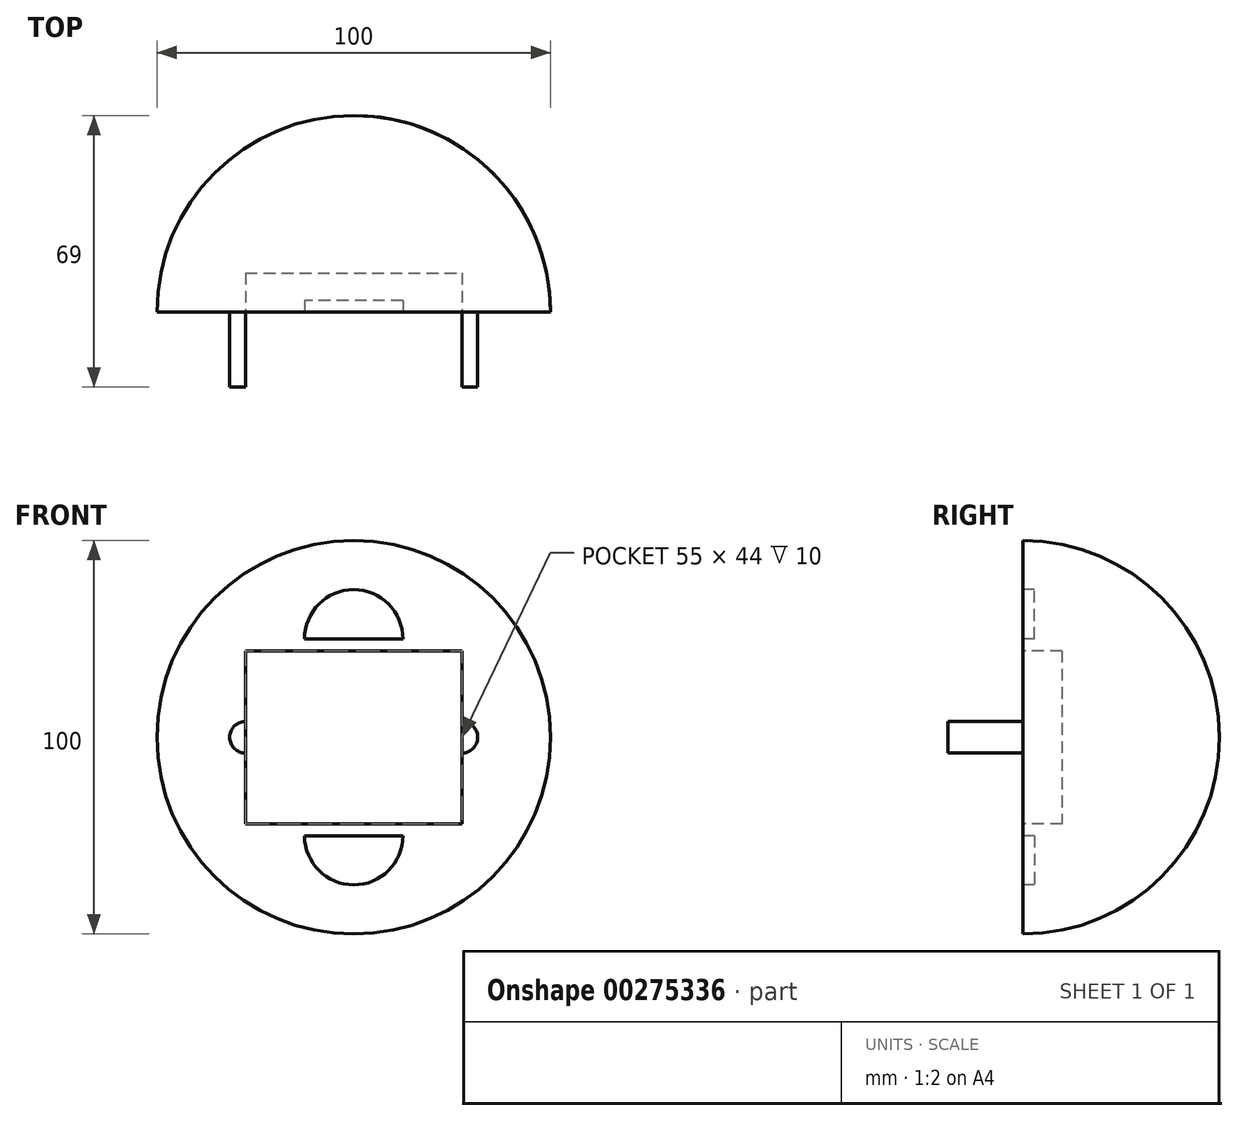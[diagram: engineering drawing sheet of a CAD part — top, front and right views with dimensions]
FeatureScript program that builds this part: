
annotation { "Feature Type Name" : "Feature", "Feature Type Description" : "" }
export const myFeature = defineFeature(function(context is Context, id is Id, definition is map)
    precondition{}
    {
        {
            var Q0;
            Q0=qCreatedBy(makeId("Top.planeOp"),FACE);
            var sketch = newSketch(context, id + "F0", { "sketchPlane" : qUnion([Q0])});
            skArc(sketch, "E0", {"start": v(0, 50) * mm, "mid": v(-35.36, 35.36) * mm, "end": v(-50, 0) * mm});
            skLineSegment(sketch, "E1", {"start": v(0, 50) * mm, "end": v(0, 0) * mm});
            skLineSegment(sketch, "E2", {"start": v(0, 0) * mm, "end": v(-50, 0) * mm});
            skSolve(sketch);
        }
        {
            var Q0;
            Q0=makeQuery(id+"F0.imprint","IMPRINT",FACE,{"disambiguationData":[TD([[makeQuery(id+"F0.imprint","IMPRINT",EDGE,{"derivedFrom":sQuery(id+"F0.wireOp",EDGE,"E0")}),1.0]])]});
            var Q1;
            Q1=sQuery(id+"F0.wireOp",EDGE,"E1");
            revolve(context, id + "F1", {"entities" : qUnion([Q0]), "axis" : qUnion([Q1]), "revolveType" : RevolveType.FULL});
        }
        {
            var Q0;
            Q0=qCreatedBy(makeId("Front.planeOp"),FACE);
            var sketch = newSketch(context, id + "F2", { "sketchPlane" : qUnion([Q0])});
            skLineSegment(sketch, "E3.bottom", {"start": v(-27.5, 22) * mm, "end": v(27.5, 22) * mm});
            skLineSegment(sketch, "E3.top", {"start": v(-27.5, -22) * mm, "end": v(27.5, -22) * mm});
            skLineSegment(sketch, "E3.left", {"start": v(-27.5, 22) * mm, "end": v(-27.5, -22) * mm});
            skLineSegment(sketch, "E3.right", {"start": v(27.5, 22) * mm, "end": v(27.5, -22) * mm});
            skPoint(sketch, "E3.middle", {"position": v(0, 0) * mm});
            skArc(sketch, "E4", {"start": v(-27.5, 4) * mm, "mid": v(-31.5, 0) * mm, "end": v(-27.5, -4) * mm});
            skPoint(sketch, "E5.center.orphan", {"position": v(27.5, 0) * mm});
            skArc(sketch, "E6", {"start": v(27.5, -4) * mm, "mid": v(31.5, 0) * mm, "end": v(27.5, 4) * mm});
            skSolve(sketch);
        }
        {
            var Q0;
            {var subQ4=sQuery(id+"F2.wireOp",EDGE,"E3.bottom");Q0=makeQuery(id+"F2.imprint","IMPRINT",FACE,{"disambiguationData":[TD([[makeQuery(id+"F2.imprint","IMPRINT",EDGE,{"derivedFrom":subQ4}),-1.0]])]});}
            extrude(context, id + "F3", {"entities" : qUnion([Q0]), "operationType" : NewBodyOperationType.REMOVE, "oppositeDirection" : true, "depth" : 10 * mm});
        }
        {
            var Q0;
            Q0=qCreatedBy(makeId("Front.planeOp"),FACE);
            var sketch = newSketch(context, id + "F4", { "sketchPlane" : qUnion([Q0])});
            skLineSegment(sketch, "E7", {"start": v(0, 0) * mm, "end": v(0, 25) * mm});
            skArc(sketch, "E8", {"start": v(12.5, 25) * mm, "mid": v(0, 37.5) * mm, "end": v(-12.5, 25) * mm});
            skLineSegment(sketch, "E9", {"start": v(0, 25) * mm, "end": v(12.5, 25) * mm});
            skLineSegment(sketch, "E10", {"start": v(0, 25) * mm, "end": v(-12.5, 25) * mm});
            skLineSegment(sketch, "E11", {"start": v(0, 0) * mm, "end": v(0, -25) * mm});
            skArc(sketch, "E12", {"start": v(-12.5, -25) * mm, "mid": v(0, -37.5) * mm, "end": v(12.5, -25) * mm});
            skLineSegment(sketch, "E13", {"start": v(0, -25) * mm, "end": v(12.5, -25) * mm});
            skLineSegment(sketch, "E14", {"start": v(0, -25) * mm, "end": v(-12.5, -25) * mm});
            skLineSegment(sketch, "E15", {"start": v(0, 0) * mm, "end": v(40, 0) * mm});
            skLineSegment(sketch, "E16", {"start": v(0, 0) * mm, "end": v(-40, 0) * mm});
            skLineSegment(sketch, "E17.top", {"start": v(-43, -10) * mm, "end": v(-37, -10) * mm});
            skLineSegment(sketch, "E17.left", {"start": v(-43, 0) * mm, "end": v(-43, -10) * mm});
            skLineSegment(sketch, "E17.right", {"start": v(-37, 0) * mm, "end": v(-37, -10) * mm});
            skPoint(sketch, "E17.middle", {"position": v(-40, 0) * mm});
            skLineSegment(sketch, "E18.top", {"start": v(37, -10) * mm, "end": v(43, -10) * mm});
            skLineSegment(sketch, "E18.left", {"start": v(37, 0) * mm, "end": v(37, -10) * mm});
            skLineSegment(sketch, "E18.right", {"start": v(43, 0) * mm, "end": v(43, -10) * mm});
            skPoint(sketch, "E18.middle", {"position": v(40, 0) * mm});
            skLineSegment(sketch, "E19", {"start": v(-40, 0) * mm, "end": v(-43, 0) * mm});
            skLineSegment(sketch, "E20", {"start": v(40, 0) * mm, "end": v(43, 0) * mm});
            skPoint(sketch, "E18.bottom.end.orphan", {"position": v(43, 10) * mm});
            skPoint(sketch, "E18.bottom.start.orphan", {"position": v(37, 10) * mm});
            skPoint(sketch, "E21.orphan", {"position": v(-37, 10) * mm});
            skPoint(sketch, "E22.orphan", {"position": v(-43, 10) * mm});
            skSolve(sketch);
        }
        {
            var Q0;
            Q0=makeQuery(id+"F4.imprint","IMPRINT",FACE,{"disambiguationData":[TD([[makeQuery(id+"F4.imprint","IMPRINT",EDGE,{"derivedFrom":sQuery(id+"F4.wireOp",EDGE,"E12")}),1.0]])]});
            var Q1;
            Q1=makeQuery(id+"F4.imprint","IMPRINT",FACE,{"disambiguationData":[TD([[makeQuery(id+"F4.imprint","IMPRINT",EDGE,{"derivedFrom":sQuery(id+"F4.wireOp",EDGE,"E8")}),1.0]])]});
            extrude(context, id + "F5", {"entities" : qUnion([Q0, Q1]), "operationType" : NewBodyOperationType.REMOVE, "oppositeDirection" : true, "depth" : 3 * mm});
        }
        {
            var Q0;
            Q0=qCreatedBy(makeId("Front.planeOp"),FACE);
            var sketch = newSketch(context, id + "F6", { "sketchPlane" : qUnion([Q0])});
            skLineSegment(sketch, "E23.bottom", {"start": v(-27.5, 22) * mm, "end": v(27.5, 22) * mm});
            skLineSegment(sketch, "E23.top", {"start": v(-27.5, -22) * mm, "end": v(27.5, -22) * mm});
            skLineSegment(sketch, "E23.left", {"start": v(-27.5, 22) * mm, "end": v(-27.5, -22) * mm});
            skLineSegment(sketch, "E23.right", {"start": v(27.5, 22) * mm, "end": v(27.5, -22) * mm});
            skPoint(sketch, "E23.middle", {"position": v(0, 0) * mm});
            skLineSegment(sketch, "E24", {"start": v(0, 0) * mm, "end": v(-27.5, 0) * mm});
            skLineSegment(sketch, "E25", {"start": v(0, 0) * mm, "end": v(27.5, 0) * mm});
            skCircle(sketch, "E26", {"center": v(-27.5, 0) * mm, "radius": 4 * mm});
            skCircle(sketch, "E27", {"center": v(27.5, 0) * mm, "radius": 4 * mm});
            skSolve(sketch);
        }
        {
            var Q0;
            {var subQ0=sQuery(id+"F6.wireOp",EDGE,"E23.left");var subQ1=makeQuery(id+"F6.imprint","INTERSECT",VERTEX,{"derivedFrom":[subQ0,sQuery(id+"F6.wireOp",EDGE,"E24")]});Q0=makeQuery(id+"F6.imprint","IMPRINT",FACE,{"disambiguationData":[TD([[makeQuery(id+"F6.imprint","IMPRINT",EDGE,{"disambiguationData":[TD([[subQ1,1.0]])],"derivedFrom":subQ0}),-1.0]])]});}
            var Q1;
            {var subQ0=sQuery(id+"F6.wireOp",EDGE,"E23.right");var subQ1=makeQuery(id+"F6.imprint","INTERSECT",VERTEX,{"derivedFrom":[subQ0,sQuery(id+"F6.wireOp",EDGE,"E25")]});Q1=makeQuery(id+"F6.imprint","IMPRINT",FACE,{"disambiguationData":[TD([[makeQuery(id+"F6.imprint","IMPRINT",EDGE,{"disambiguationData":[TD([[subQ1,1.0]])],"derivedFrom":subQ0}),1.0]])]});}
            extrude(context, id + "F7", {"entities" : qUnion([Q0, Q1]), "operationType" : NewBodyOperationType.ADD, "depth" : 19 * mm});
        }
    });
